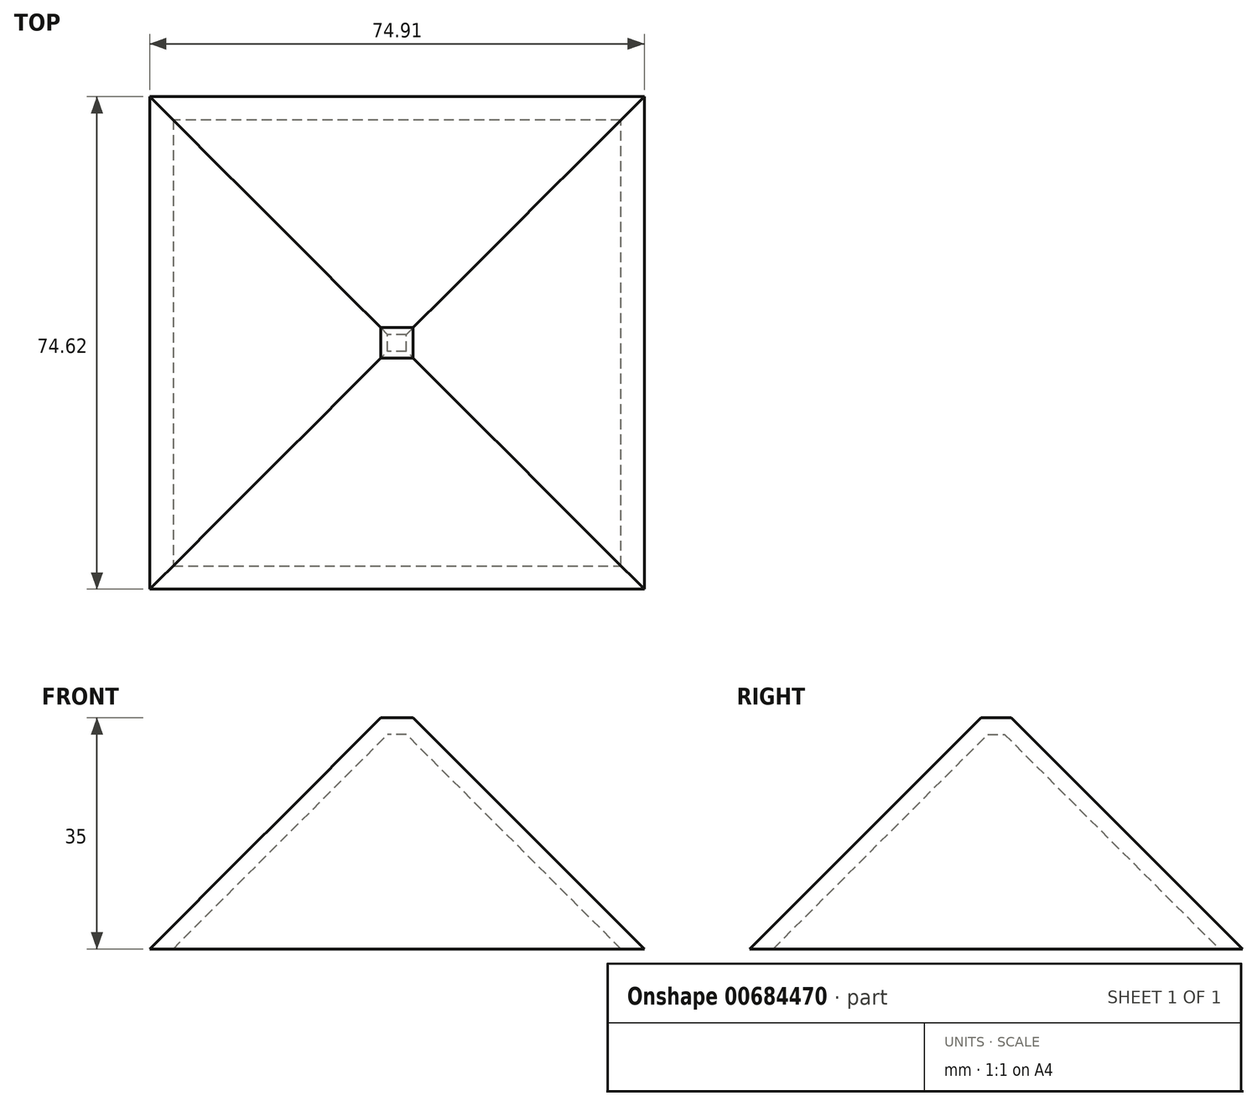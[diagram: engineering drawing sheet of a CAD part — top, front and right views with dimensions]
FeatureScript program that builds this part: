
annotation { "Feature Type Name" : "Feature", "Feature Type Description" : "" }
export const myFeature = defineFeature(function(context is Context, id is Id, definition is map)
    precondition{}
    {
        {
            var Q0;
            Q0=qCreatedBy(makeId("Top.planeOp"),FACE);
            var sketch = newSketch(context, id + "F0", { "sketchPlane" : qUnion([Q0])});
            skLineSegment(sketch, "E0.bottom", {"start": v(0, 0) * mm, "end": v(-74.9, 0) * mm});
            skLineSegment(sketch, "E0.top", {"start": v(0, 74.62) * mm, "end": v(-74.9, 74.62) * mm});
            skLineSegment(sketch, "E0.left", {"start": v(0, 0) * mm, "end": v(0, 74.62) * mm});
            skLineSegment(sketch, "E0.right", {"start": v(-74.9, 0) * mm, "end": v(-74.9, 74.62) * mm});
            skSolve(sketch);
        }
        {
            var Q0;
            Q0 = qSketchRegion(id + "F0", true);
            extrude(context, id + "F1", {"entities" : qUnion([Q0]), "depth" : 5 * mm, "offsetDistance" : 25 * mm});
        }
        {
            var Q0;
            Q0=makeQuery(id+"F1.opExtrude","CAP_EDGE",EDGE,{"disambiguationData":[OSD([sQuery(id+"F0.wireOp",EDGE,"E0.right")])],"isStart":false});
            var Q1;
            Q1=makeQuery(id+"F1.opExtrude","CAP_FACE",FACE,{"disambiguationData":[OSD([sQuery(id+"F0.wireOp",EDGE,"E0.bottom"),sQuery(id+"F0.wireOp",EDGE,"E0.top"),sQuery(id+"F0.wireOp",EDGE,"E0.left"),sQuery(id+"F0.wireOp",EDGE,"E0.right")])],"isStart":false});
            chamfer(context, id + "F2", {"entities" : qUnion([Q0, Q1]), "width" : 5 * mm, "tangentPropagation" : true});
        }
        {
            var Q0;
            Q0=makeQuery(id+"F1.opExtrude","CAP_FACE",FACE,{"disambiguationData":[OSD([sQuery(id+"F0.wireOp",EDGE,"E0.bottom"),sQuery(id+"F0.wireOp",EDGE,"E0.top"),sQuery(id+"F0.wireOp",EDGE,"E0.left"),sQuery(id+"F0.wireOp",EDGE,"E0.right")])],"isStart":false});
            var sketch = newSketch(context, id + "F3", { "sketchPlane" : qUnion([Q0])});
            skLineSegment(sketch, "E1.bottom", {"start": v(-69.9, 69.62) * mm, "end": v(-5, 69.62) * mm});
            skLineSegment(sketch, "E1.top", {"start": v(-69.9, 5) * mm, "end": v(-5, 5) * mm});
            skLineSegment(sketch, "E1.left", {"start": v(-69.9, 69.62) * mm, "end": v(-69.9, 5) * mm});
            skLineSegment(sketch, "E1.right", {"start": v(-5, 69.62) * mm, "end": v(-5, 5) * mm});
            skSolve(sketch);
        }
        {
            var Q0;
            Q0=makeQuery(id+"F3.imprint","IMPRINT",FACE,{"disambiguationData":[TD([[makeQuery(id+"F3.imprint","IMPRINT",EDGE,{"derivedFrom":sQuery(id+"F3.wireOp",EDGE,"E1.bottom")}),1.0]])]});
            extrude(context, id + "F4", {"entities" : qUnion([Q0]), "operationType" : NewBodyOperationType.ADD, "depth" : 5 * mm, "offsetDistance" : 25 * mm});
        }
        {
            var Q0;
            Q0=makeQuery(id+"F4.opExtrude","CAP_FACE",FACE,{"disambiguationData":[OSD([sQuery(id+"F3.wireOp",EDGE,"E1.bottom"),sQuery(id+"F3.wireOp",EDGE,"E1.top"),sQuery(id+"F3.wireOp",EDGE,"E1.left"),sQuery(id+"F3.wireOp",EDGE,"E1.right")])],"isStart":false});
            chamfer(context, id + "F5", {"entities" : qUnion([Q0]), "width" : 5 * mm, "tangentPropagation" : true});
        }
        {
            var Q0;
            Q0=makeQuery(id+"F4.opExtrude","CAP_FACE",FACE,{"disambiguationData":[OSD([sQuery(id+"F3.wireOp",EDGE,"E1.bottom"),sQuery(id+"F3.wireOp",EDGE,"E1.top"),sQuery(id+"F3.wireOp",EDGE,"E1.left"),sQuery(id+"F3.wireOp",EDGE,"E1.right")])],"isStart":false});
            var sketch = newSketch(context, id + "F6", { "sketchPlane" : qUnion([Q0])});
            skLineSegment(sketch, "E2.bottom", {"start": v(-64.9, 64.62) * mm, "end": v(-10, 64.62) * mm});
            skLineSegment(sketch, "E2.top", {"start": v(-64.9, 10) * mm, "end": v(-10, 10) * mm});
            skLineSegment(sketch, "E2.left", {"start": v(-64.9, 64.62) * mm, "end": v(-64.9, 10) * mm});
            skLineSegment(sketch, "E2.right", {"start": v(-10, 64.62) * mm, "end": v(-10, 10) * mm});
            skSolve(sketch);
        }
        {
            var Q0;
            Q0 = qSketchRegion(id + "F6", true);
            extrude(context, id + "F7", {"entities" : qUnion([Q0]), "operationType" : NewBodyOperationType.ADD, "depth" : 5 * mm, "offsetDistance" : 25 * mm});
        }
        {
            var Q0;
            Q0=makeQuery(id+"F7.opExtrude","CAP_FACE",FACE,{"disambiguationData":[OSD([sQuery(id+"F6.wireOp",EDGE,"E2.bottom"),sQuery(id+"F6.wireOp",EDGE,"E2.top"),sQuery(id+"F6.wireOp",EDGE,"E2.left"),sQuery(id+"F6.wireOp",EDGE,"E2.right")])],"isStart":false});
            chamfer(context, id + "F8", {"entities" : qUnion([Q0]), "width" : 5 * mm, "tangentPropagation" : true});
        }
        {
            var Q0;
            Q0=makeQuery(id+"F7.opExtrude","CAP_FACE",FACE,{"disambiguationData":[OSD([sQuery(id+"F6.wireOp",EDGE,"E2.bottom"),sQuery(id+"F6.wireOp",EDGE,"E2.top"),sQuery(id+"F6.wireOp",EDGE,"E2.left"),sQuery(id+"F6.wireOp",EDGE,"E2.right")])],"isStart":false});
            var sketch = newSketch(context, id + "F9", { "sketchPlane" : qUnion([Q0])});
            skLineSegment(sketch, "E3.bottom", {"start": v(-59.9, 59.62) * mm, "end": v(-15, 59.62) * mm});
            skLineSegment(sketch, "E3.top", {"start": v(-59.9, 15) * mm, "end": v(-15, 15) * mm});
            skLineSegment(sketch, "E3.left", {"start": v(-59.9, 59.62) * mm, "end": v(-59.9, 15) * mm});
            skLineSegment(sketch, "E3.right", {"start": v(-15, 59.62) * mm, "end": v(-15, 15) * mm});
            skSolve(sketch);
        }
        {
            var Q0;
            Q0 = qSketchRegion(id + "F9", true);
            extrude(context, id + "F10", {"entities" : qUnion([Q0]), "operationType" : NewBodyOperationType.ADD, "depth" : 5 * mm, "offsetDistance" : 25 * mm});
        }
        {
            var Q0;
            Q0=makeQuery(id+"F10.opExtrude","CAP_FACE",FACE,{"disambiguationData":[OSD([sQuery(id+"F9.wireOp",EDGE,"E3.bottom"),sQuery(id+"F9.wireOp",EDGE,"E3.top"),sQuery(id+"F9.wireOp",EDGE,"E3.left"),sQuery(id+"F9.wireOp",EDGE,"E3.right")])],"isStart":false});
            chamfer(context, id + "F11", {"entities" : qUnion([Q0]), "width" : 5 * mm, "tangentPropagation" : true});
        }
        {
            var Q0;
            Q0=makeQuery(id+"F10.opExtrude","CAP_FACE",FACE,{"disambiguationData":[OSD([sQuery(id+"F9.wireOp",EDGE,"E3.bottom"),sQuery(id+"F9.wireOp",EDGE,"E3.top"),sQuery(id+"F9.wireOp",EDGE,"E3.left"),sQuery(id+"F9.wireOp",EDGE,"E3.right")])],"isStart":false});
            var sketch = newSketch(context, id + "F12", { "sketchPlane" : qUnion([Q0])});
            skLineSegment(sketch, "E4.bottom", {"start": v(-54.9, 54.62) * mm, "end": v(-20, 54.62) * mm});
            skLineSegment(sketch, "E4.top", {"start": v(-54.9, 20) * mm, "end": v(-20, 20) * mm});
            skLineSegment(sketch, "E4.left", {"start": v(-54.9, 54.62) * mm, "end": v(-54.9, 20) * mm});
            skLineSegment(sketch, "E4.right", {"start": v(-20, 54.62) * mm, "end": v(-20, 20) * mm});
            skSolve(sketch);
        }
        {
            var Q0;
            Q0 = qSketchRegion(id + "F12", true);
            extrude(context, id + "F13", {"entities" : qUnion([Q0]), "operationType" : NewBodyOperationType.ADD, "depth" : 5 * mm, "offsetDistance" : 25 * mm});
        }
        {
            var Q0;
            Q0=makeQuery(id+"F13.opExtrude","CAP_FACE",FACE,{"disambiguationData":[OSD([sQuery(id+"F12.wireOp",EDGE,"E4.bottom"),sQuery(id+"F12.wireOp",EDGE,"E4.top"),sQuery(id+"F12.wireOp",EDGE,"E4.left"),sQuery(id+"F12.wireOp",EDGE,"E4.right")])],"isStart":false});
            chamfer(context, id + "F14", {"entities" : qUnion([Q0]), "width" : 5 * mm, "tangentPropagation" : true});
        }
        {
            var Q0;
            Q0=makeQuery(id+"F13.opExtrude","CAP_FACE",FACE,{"disambiguationData":[OSD([sQuery(id+"F12.wireOp",EDGE,"E4.bottom"),sQuery(id+"F12.wireOp",EDGE,"E4.top"),sQuery(id+"F12.wireOp",EDGE,"E4.left"),sQuery(id+"F12.wireOp",EDGE,"E4.right")])],"isStart":false});
            var sketch = newSketch(context, id + "F15", { "sketchPlane" : qUnion([Q0])});
            skLineSegment(sketch, "E5.bottom", {"start": v(-49.9, 49.62) * mm, "end": v(-25, 49.62) * mm});
            skLineSegment(sketch, "E5.top", {"start": v(-49.9, 25) * mm, "end": v(-25, 25) * mm});
            skLineSegment(sketch, "E5.left", {"start": v(-49.9, 49.62) * mm, "end": v(-49.9, 25) * mm});
            skLineSegment(sketch, "E5.right", {"start": v(-25, 49.62) * mm, "end": v(-25, 25) * mm});
            skSolve(sketch);
        }
        {
            var Q0;
            Q0 = qSketchRegion(id + "F15", true);
            extrude(context, id + "F16", {"entities" : qUnion([Q0]), "operationType" : NewBodyOperationType.ADD, "depth" : 5 * mm, "offsetDistance" : 25 * mm});
        }
        {
            var Q0;
            Q0=makeQuery(id+"F16.opExtrude","CAP_FACE",FACE,{"disambiguationData":[OSD([sQuery(id+"F15.wireOp",EDGE,"E5.bottom"),sQuery(id+"F15.wireOp",EDGE,"E5.top"),sQuery(id+"F15.wireOp",EDGE,"E5.left"),sQuery(id+"F15.wireOp",EDGE,"E5.right")])],"isStart":false});
            chamfer(context, id + "F17", {"entities" : qUnion([Q0]), "width" : 5 * mm, "tangentPropagation" : true});
        }
        {
            var Q0;
            Q0=makeQuery(id+"F16.opExtrude","CAP_FACE",FACE,{"disambiguationData":[OSD([sQuery(id+"F15.wireOp",EDGE,"E5.bottom"),sQuery(id+"F15.wireOp",EDGE,"E5.top"),sQuery(id+"F15.wireOp",EDGE,"E5.left"),sQuery(id+"F15.wireOp",EDGE,"E5.right")])],"isStart":false});
            var sketch = newSketch(context, id + "F18", { "sketchPlane" : qUnion([Q0])});
            skLineSegment(sketch, "E6.bottom", {"start": v(-44.9, 44.62) * mm, "end": v(-30, 44.62) * mm});
            skLineSegment(sketch, "E6.top", {"start": v(-44.9, 30) * mm, "end": v(-30, 30) * mm});
            skLineSegment(sketch, "E6.left", {"start": v(-44.9, 44.62) * mm, "end": v(-44.9, 30) * mm});
            skLineSegment(sketch, "E6.right", {"start": v(-30, 44.62) * mm, "end": v(-30, 30) * mm});
            skSolve(sketch);
        }
        {
            var Q0;
            Q0 = qSketchRegion(id + "F18", true);
            extrude(context, id + "F19", {"entities" : qUnion([Q0]), "operationType" : NewBodyOperationType.ADD, "depth" : 5 * mm, "offsetDistance" : 25 * mm});
        }
        {
            var Q0;
            Q0=makeQuery(id+"F19.opExtrude","CAP_FACE",FACE,{"disambiguationData":[OSD([sQuery(id+"F18.wireOp",EDGE,"E6.bottom"),sQuery(id+"F18.wireOp",EDGE,"E6.top"),sQuery(id+"F18.wireOp",EDGE,"E6.left"),sQuery(id+"F18.wireOp",EDGE,"E6.right")])],"isStart":false});
            chamfer(context, id + "F20", {"entities" : qUnion([Q0]), "width" : 5 * mm, "tangentPropagation" : true});
        }
        {
            var Q0;
            Q0=makeQuery(id+"F1.opExtrude","CAP_FACE",FACE,{"disambiguationData":[OSD([sQuery(id+"F0.wireOp",EDGE,"E0.bottom"),sQuery(id+"F0.wireOp",EDGE,"E0.top"),sQuery(id+"F0.wireOp",EDGE,"E0.left"),sQuery(id+"F0.wireOp",EDGE,"E0.right")])],"isStart":true});
            shell(context, id + "F21", {"entities" : qUnion([Q0]), "thickness" : 2.5 * mm});
        }
    });
